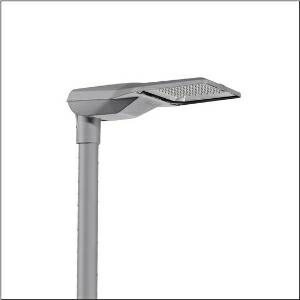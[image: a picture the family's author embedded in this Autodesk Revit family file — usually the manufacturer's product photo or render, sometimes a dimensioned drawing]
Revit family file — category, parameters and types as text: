
# Revit family: streetlight_sl_21_iq_midi___st0_5a_5xe3b41d08mb_eec4
name_source: partatom
category: Lighting Fixtures
units: mm (PartAtom-declared; Revit-internal decimal feet)

## family parameters
Cut with Voids When Loaded = No
Host = Face
Light Source = No
Part Type = Normal
Room Calculation Point = No
Round Connector Dimension = Use Diameter
Shared = No

## types (1)
- --- (1 x LED, 20360 lm, 146.7 W, 4000K)
    Apparent Load = 147 VA
    CIE Flux Codes = 41 75 97 100 100
    Color Rendering = 70
    Color Temperature = 4000K
    Default Elevation = 1800 mm
    Description = Streetlight SL 21 iQ midi, mast luminaire, primary light control with lens, of PMMA, primary optical cover: cover, of toughened safety glass, transparent, light distribution: ST0.5a, light emission: direct distribution, primary light characteristic: asymmetric, installation type: post-top, side-entry, LED, High Power LED, rated luminous flux: 20.360lm, luminous efficacy: 139lm/W, light colour: 740, colour temperature: 4000K, control gear: iQ-Comfort, control: Auto-Match, Temp-Guard, Lumen-Switch, Night-Set, Smart-Wire, Light-Fading, Desk-Remote (wireless, voltage-free reading and setting of iQ features in the workshop via application-optimized NFC function/RFID function), optimised constant luminous flux control (CLO 2.0), pre-setting: linear dimming characteristic, mains connection: 230..240V, AC, 50/60Hz, start of lifetime: 147W, end of service life: 161W, reduction: 62W, luminaire housing, of diecast aluminium, powder-coated, SITECO metallic grey (DB 702S), corrosivity category C5 high according to DIN EN ISO 12944, please order mast flange separately, inclination adjustable: 0°, 5°, 10°, 15°, sealing non-destructively replaceable, multi-level sealing system, length: 644mm, width: 335mm, height: 110mm, mast flange for spigot size: 42mm (side-entry): 5XC10008XM4, 60/48mm (side-entry/post-top): 5XC10108XM2, 76/60mm (side-entry/post-top): 5XC10108XM1, mounting height: 4..8m, protection rating (complete): IP66, insulation class (complete): insulation class II (safety insulation), certification: CE, ENEC, ENEC+, VDE, impact resistance: IK10, permissible operating ambient temperature for outdoor applications: -40..+50°C, standard-compliant lighting for roads and squares, packaging unit: 1 piece

Light Distribution: ST0.5a
    Height = 111 mm
    Lamp = 1 x LED
    Lamp Light Flux = 20360 lm
    Lamp Power = 146.7 W
    Lamp count = 1
    Length = 644 mm
    Luminous efficacy = 139 lm/W
    Manufacturer = Siteco
    ModVariant = No
    Model = 5XE3B41D08MB
    Number of Poles = 1
    OnlyDefault = Yes
    Power Factor = 1
    Product Name = Streetlight SL 21 iQ midi | ST0.5a
    Product group = mast luminaire | pylon top
    ProductGroupID = 6100
    Protection Class = Protection class II
    Protection Degree = IP 66
    RLX_Detail_Level = 1
    RLX_Emergency_Light_Flux = 0 lm
    RLX_Emergency_Type = 0
    RLX_Emergency_Type_DB = No
    RlxData = <blob elided: 37945 chars, md5=5a7e0eb6>
    Socket = socket
    Standby Power = 0 W
    System Light Flux = 20360 lm
    System Power = 147 W
    Type Comments = factory setting: luminous flux: 100 % | dim-lin: 254 | 753 mA
    Type Image = l_1004298.jpg
    URL = http://relux.com
    VarID = @adj_189261
    Voltage = 0 V
    Weight = 0.00 kg
    Width = 336 mm

## geometry (parser evidence)
native form markers: Blend x4, Sweep x10
no freeform markers — native parametric forms only
